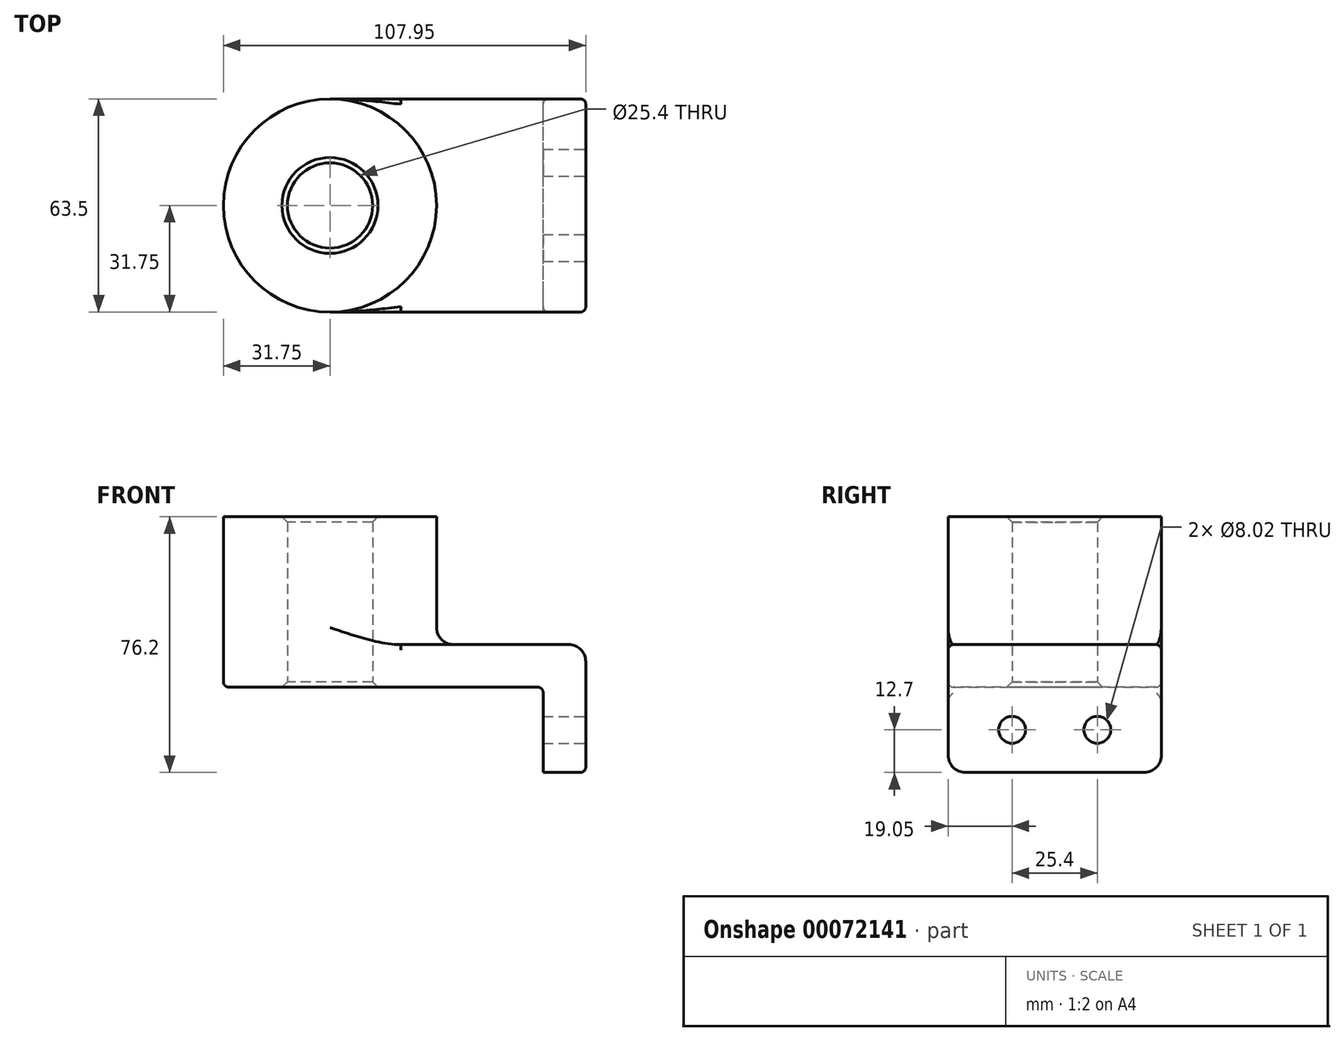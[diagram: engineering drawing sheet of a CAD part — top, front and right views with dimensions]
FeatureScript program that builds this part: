
annotation { "Feature Type Name" : "Feature", "Feature Type Description" : "" }
export const myFeature = defineFeature(function(context is Context, id is Id, definition is map)
    precondition{}
    {
        {
            var Q0;
            Q0=qCreatedBy(makeId("Top.planeOp"),FACE);
            var sketch = newSketch(context, id + "F0", { "sketchPlane" : qUnion([Q0])});
            skLineSegment(sketch, "E0.rect.bottom", {"start": v(38.1, -31.75) * mm, "end": v(-38.1, -31.75) * mm});
            skLineSegment(sketch, "E0.rect.top", {"start": v(38.1, 31.75) * mm, "end": v(-38.1, 31.75) * mm});
            skLineSegment(sketch, "E0.rect.left", {"start": v(38.1, -31.75) * mm, "end": v(38.1, 31.75) * mm});
            skLineSegment(sketch, "E0.rect.right", {"start": v(-38.1, -31.75) * mm, "end": v(-38.1, 31.75) * mm});
            skPoint(sketch, "E0.rect.middle", {"position": v(0, 0) * mm});
            skCircle(sketch, "E1", {"center": v(-38.1, 0) * mm, "radius": 31.75 * mm});
            skCircle(sketch, "E2", {"center": v(-38.1, 0) * mm, "radius": 12.7 * mm});
            skSolve(sketch);
        }
        {
            var Q0;
            Q0 = qSketchRegion(id + "F0", true);
            extrude(context, id + "F1", {"entities" : qUnion([Q0]), "depth" : 12.7 * mm});
        }
        {
            var Q0;
            {var subQ1=sQuery(id+"F0.wireOp",EDGE,"E0.rect.right");var subQ3=sQuery(id+"F0.wireOp",EDGE,"E2");var subQ4=makeQuery(id+"F0.imprint","INTERSECT",VERTEX,{"disambiguationData":[OD(0.0)],"derivedFrom":[subQ1,subQ3]});Q0=makeQuery(id+"F0.imprint","IMPRINT",FACE,{"disambiguationData":[TD([[makeQuery(id+"F0.imprint","IMPRINT",EDGE,{"disambiguationData":[TD([[subQ4,-1.0]])],"derivedFrom":subQ3}),-1.0]])]});}
            var Q1;
            {var subQ1=sQuery(id+"F0.wireOp",EDGE,"E0.rect.right");var subQ3=sQuery(id+"F0.wireOp",EDGE,"E2");var subQ4=makeQuery(id+"F0.imprint","INTERSECT",VERTEX,{"disambiguationData":[OD(0.0)],"derivedFrom":[subQ1,subQ3]});Q1=makeQuery(id+"F0.imprint","IMPRINT",FACE,{"disambiguationData":[TD([[makeQuery(id+"F0.imprint","IMPRINT",EDGE,{"disambiguationData":[TD([[subQ4,1.0]])],"derivedFrom":subQ3}),-1.0]])]});}
            extrude(context, id + "F2", {"entities" : qUnion([Q0, Q1]), "operationType" : NewBodyOperationType.ADD, "depth" : 50.8 * mm});
        }
        {
            var Q0;
            Q0=makeQuery(id+"F1.opExtrude","SWEPT_FACE",FACE,{"disambiguationData":[OSD([sQuery(id+"F0.wireOp",EDGE,"E0.rect.left")])]});
            var sketch = newSketch(context, id + "F3", { "sketchPlane" : qUnion([Q0])});
            skLineSegment(sketch, "E3.bottom", {"start": v(-31.75, 12.7) * mm, "end": v(31.75, 12.7) * mm});
            skLineSegment(sketch, "E3.top", {"start": v(-31.75, -25.4) * mm, "end": v(31.75, -25.4) * mm});
            skLineSegment(sketch, "E3.left", {"start": v(-31.75, 12.7) * mm, "end": v(-31.75, -25.4) * mm});
            skLineSegment(sketch, "E3.right", {"start": v(31.75, 12.7) * mm, "end": v(31.75, -25.4) * mm});
            skLineSegment(sketch, "E4", {"start": v(0, 0) * mm, "end": v(0, -25.4) * mm});
            skCircle(sketch, "E5", {"center": v(-12.7, -12.7) * mm, "radius": 4 * mm});
            skCircle(sketch, "E6.MirrorC", {"center": v(12.7, -12.7) * mm, "radius": 4 * mm});
            skSolve(sketch);
        }
        {
            var Q0;
            Q0 = qSketchRegion(id + "F3", true);
            extrude(context, id + "F4", {"entities" : qUnion([Q0]), "operationType" : NewBodyOperationType.ADD, "oppositeDirection" : true, "depth" : 12.7 * mm});
        }
        {
            var Q0;
            {var subQ0=sQuery(id+"F0.wireOp",EDGE,"E1");Q0=makeQuery(id+"F2.boolean.opBoolean","INTERSECT",EDGE,{"derivedFrom":[makeQuery(id+"F1.opExtrude","CAP_FACE",FACE,{"disambiguationData":[OSD([sQuery(id+"F0.wireOp",EDGE,"E0.rect.bottom"),sQuery(id+"F0.wireOp",EDGE,"E0.rect.top"),sQuery(id+"F0.wireOp",EDGE,"E0.rect.left"),subQ0,sQuery(id+"F0.wireOp",EDGE,"E2")])],"isStart":false}),makeQuery(id+"F2.opExtrude","SWEPT_FACE",FACE,{"disambiguationData":[OSD([subQ0])]})]});}
            var Q1;
            Q1=makeQuery(id+"F1.opExtrude","CAP_EDGE",EDGE,{"disambiguationData":[OSD([sQuery(id+"F0.wireOp",EDGE,"E0.rect.left")])],"isStart":false});
            var Q2;
            Q2=makeQuery(id+"F4.opExtrude","SWEPT_EDGE",EDGE,{"disambiguationData":[OSD([sQuery(id+"F3.wireOp",EDGE,"E3.top"),sQuery(id+"F3.wireOp",EDGE,"E3.left")])]});
            var Q3;
            Q3=makeQuery(id+"F4.opExtrude","SWEPT_EDGE",EDGE,{"disambiguationData":[OSD([sQuery(id+"F3.wireOp",EDGE,"E3.top"),sQuery(id+"F3.wireOp",EDGE,"E3.right")])]});
            fillet(context, id + "F5", {"entities" : qUnion([Q0, Q1, Q2, Q3]), "radius" : 5.08 * mm, "tangentPropagation" : true, "allowEdgeOverflow" : false});
        }
        {
            var Q0;
            Q0=makeQuery(id+"F1.opExtrude","CAP_EDGE",EDGE,{"disambiguationData":[OSD([sQuery(id+"F0.wireOp",EDGE,"E0.rect.top")])],"isStart":false});
            var Q1;
            Q1=makeQuery(id+"F1.opExtrude","CAP_EDGE",EDGE,{"disambiguationData":[OSD([sQuery(id+"F0.wireOp",EDGE,"E0.rect.top")])],"isStart":true});
            var Q2;
            Q2=makeQuery(id+"F4.boolean.opBoolean","INTERSECT",EDGE,{"derivedFrom":[makeQuery(id+"F1.opExtrude","CAP_FACE",FACE,{"disambiguationData":[OSD([sQuery(id+"F0.wireOp",EDGE,"E0.rect.bottom"),sQuery(id+"F0.wireOp",EDGE,"E0.rect.top"),sQuery(id+"F0.wireOp",EDGE,"E0.rect.left"),sQuery(id+"F0.wireOp",EDGE,"E1"),sQuery(id+"F0.wireOp",EDGE,"E2")])],"isStart":true}),makeQuery(id+"F4.opExtrude","CAP_FACE",FACE,{"disambiguationData":[OSD([sQuery(id+"F3.wireOp",EDGE,"E3.bottom"),sQuery(id+"F3.wireOp",EDGE,"E3.top"),sQuery(id+"F3.wireOp",EDGE,"E3.left"),sQuery(id+"F3.wireOp",EDGE,"E3.right"),sQuery(id+"F3.wireOp",EDGE,"E5"),sQuery(id+"F3.wireOp",EDGE,"E6.MirrorC")])],"isStart":false})]});
            var Q3;
            Q3=makeQuery(id+"F1.opExtrude","CAP_EDGE",EDGE,{"disambiguationData":[OSD([sQuery(id+"F0.wireOp",EDGE,"E0.rect.bottom")])],"isStart":true});
            var Q4;
            Q4=makeQuery(id+"F1.opExtrude","CAP_EDGE",EDGE,{"disambiguationData":[OSD([sQuery(id+"F0.wireOp",EDGE,"E0.rect.bottom")])],"isStart":false});
            fillet(context, id + "F6", {"entities" : qUnion([Q0, Q1, Q2, Q3, Q4]), "radius" : 1.59 * mm, "tangentPropagation" : true, "allowEdgeOverflow" : false});
        }
        {
            var Q0;
            {var subQ0=sQuery(id+"F0.wireOp",EDGE,"E2");Q0=makeQuery(id+"F2.boolean.opBoolean","MERGE",FACE,{"derivedFrom":[makeQuery(id+"F1.opExtrude","SWEPT_FACE",FACE,{"disambiguationData":[OSD([subQ0])]}),makeQuery(id+"F2.opExtrude","SWEPT_FACE",FACE,{"disambiguationData":[OSD([subQ0])]})]});}
            chamfer(context, id + "F7", {"entities" : qUnion([Q0]), "width" : 1.59 * mm, "tangentPropagation" : true});
        }
    });
